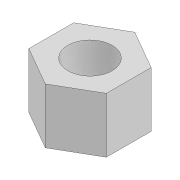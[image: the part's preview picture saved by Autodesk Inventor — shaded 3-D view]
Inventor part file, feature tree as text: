
AUTODESK INVENTOR PART (.ipt)
format: ipt  version: 2022 (Build 260153000, 153)  size: 83,968 bytes
history: native  units: mm
features: extrude x1, sketch x1
ambient origin geometry x8: Origin, YZ Plane, XZ Plane, XY Plane, X Axis, Y Axis, Z Axis, Center Point
bodies: Solid1 (feature_tree)
feature tree (2):
  extrude  "Extrusion1"  Depth=5.0mm
  sketch  "Sketch1"  dims[d0=7.0mm d1=4.0mm d2=5.0mm d3=0.0mm]
